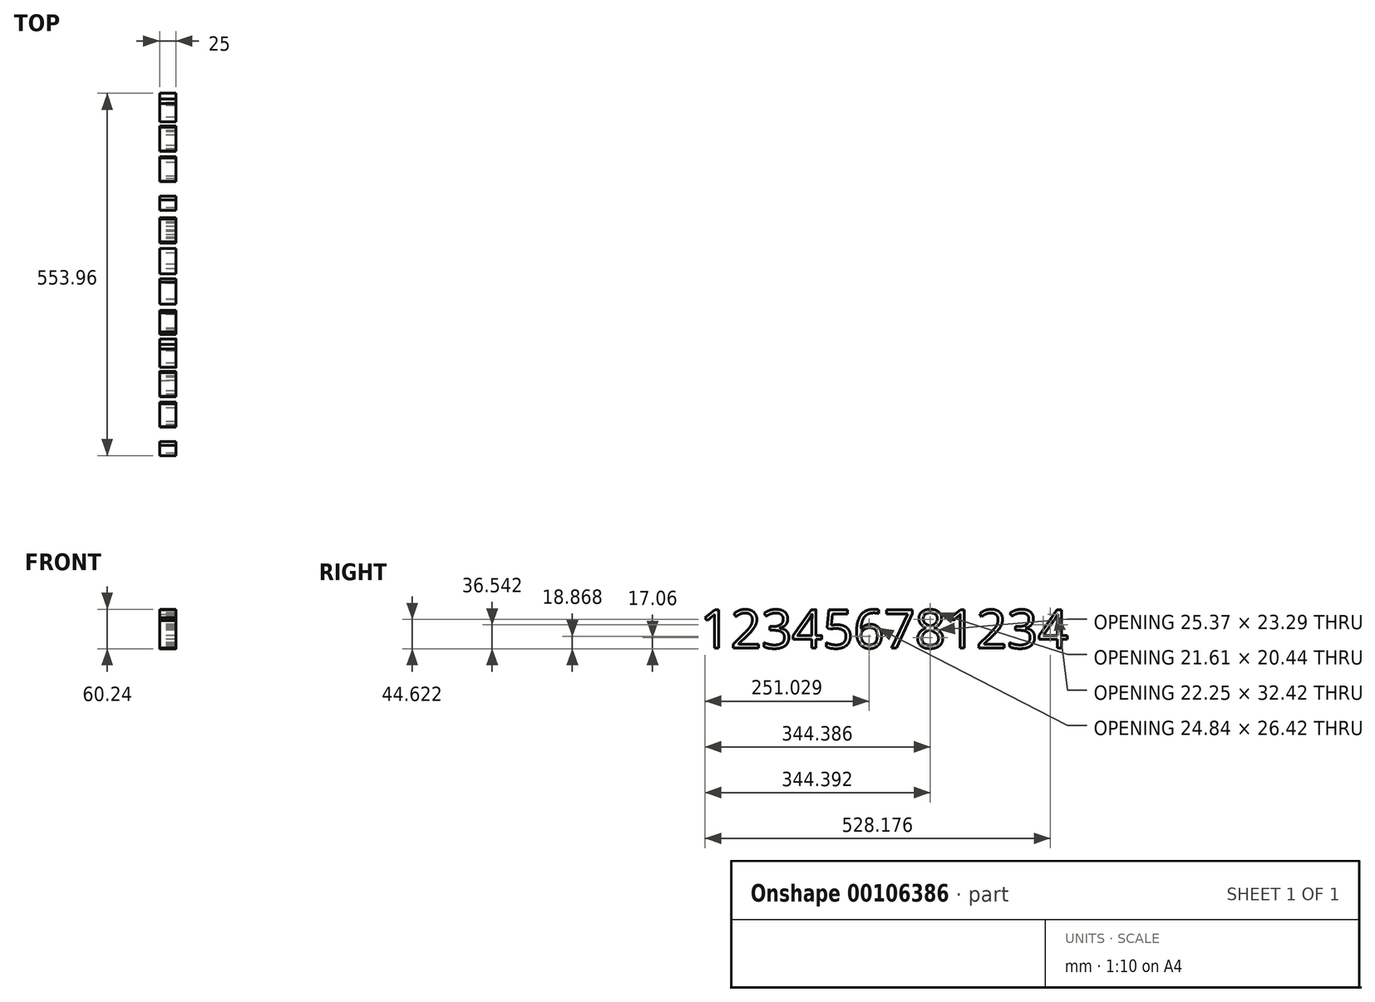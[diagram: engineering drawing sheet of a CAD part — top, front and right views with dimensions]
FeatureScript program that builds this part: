
annotation { "Feature Type Name" : "Feature", "Feature Type Description" : "" }
export const myFeature = defineFeature(function(context is Context, id is Id, definition is map)
    precondition{}
    {
        {
            var Q0;
            Q0=qCreatedBy(makeId("Right.planeOp"),FACE);
            var sketch = newSketch(context, id + "F0", { "sketchPlane" : qUnion([Q0])});
            skText(sketch, "E0", { "text": "123456781234", "fontName": "OpenSans-Regular.ttf"});
            const initialGuessF0  = {"E0": [-0.23107, -0.0591, 1, 0, 0.0591]};
            skSetInitialGuess(sketch, initialGuessF0);
            skSolve(sketch);
        }
        {
            var Q0;
            Q0 = qSketchRegion(id + "F0", true);
            extrude(context, id + "F1", {"entities" : qUnion([Q0]), "depth" : 25 * mm});
        }
        {
            var Q0;
            Q0=makeQuery(id+"F1.opExtrude","SWEPT_FACE",FACE,{"disambiguationData":[OSD([sQuery(id+"F0.wireOp",EDGE,"E0.sketch_text.stroke-32")])]});
            var Q1;
            Q1=makeQuery(id+"F1.opExtrude","CAP_FACE",FACE,{"disambiguationData":[OSD([sQuery(id+"F0.wireOp",EDGE,"E0.sketch_text.stroke-57"),sQuery(id+"F0.wireOp",EDGE,"E0.sketch_text.stroke-58"),sQuery(id+"F0.wireOp",EDGE,"E0.sketch_text.stroke-59"),sQuery(id+"F0.wireOp",EDGE,"E0.sketch_text.stroke-60"),sQuery(id+"F0.wireOp",EDGE,"E0.sketch_text.stroke-61"),sQuery(id+"F0.wireOp",EDGE,"E0.sketch_text.stroke-62"),sQuery(id+"F0.wireOp",EDGE,"E0.sketch_text.stroke-63"),sQuery(id+"F0.wireOp",EDGE,"E0.sketch_text.stroke-64"),sQuery(id+"F0.wireOp",EDGE,"E0.sketch_text.stroke-65"),sQuery(id+"F0.wireOp",EDGE,"E0.sketch_text.stroke-66"),sQuery(id+"F0.wireOp",EDGE,"E0.sketch_text.stroke-67"),sQuery(id+"F0.wireOp",EDGE,"E0.sketch_text.stroke-68"),sQuery(id+"F0.wireOp",EDGE,"E0.sketch_text.stroke-69"),sQuery(id+"F0.wireOp",EDGE,"E0.sketch_text.stroke-70"),sQuery(id+"F0.wireOp",EDGE,"E0.sketch_text.stroke-71"),sQuery(id+"F0.wireOp",EDGE,"E0.sketch_text.stroke-72"),sQuery(id+"F0.wireOp",EDGE,"E0.sketch_text.stroke-73")])],"isStart":false});
            fillet(context, id + "F2", {"entities" : qUnion([Q0, Q1]), "radius" : .1 * mm, "tangentPropagation" : true, "allowEdgeOverflow" : false});
        }
    });
